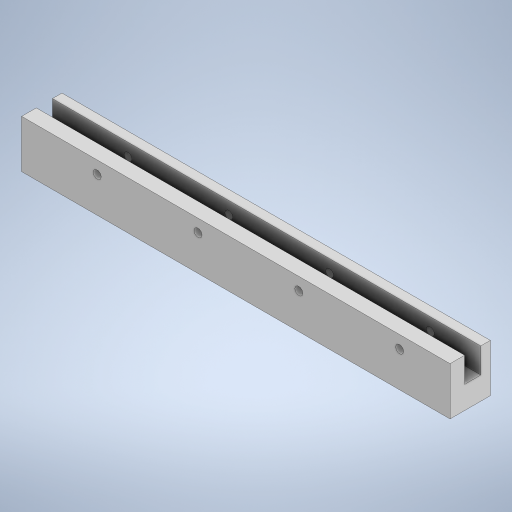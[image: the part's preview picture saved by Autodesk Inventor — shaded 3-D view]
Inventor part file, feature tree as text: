
AUTODESK INVENTOR PART (.ipt)
format: ipt  version: 2023 (Build 270158000, 158)  size: 327,680 bytes
history: native  units: mm
features: sketch x11, extrude x7, hole x4, other x1
ambient origin geometry x8: Origin, YZ Plane, XZ Plane, XY Plane, X Axis, Y Axis, Z Axis, Center Point
bodies: Body1 (feature_tree)
feature tree (23):
  other  "ソリッド1"
  extrude  "押し出し1"  Depth=180.0mm
  extrude  "押し出し2"  Depth=6.0mm
  extrude  "押し出し3"  Depth=17.0mm TaperAngle=0.0deg
  extrude  "押し出し4"  Depth=170.0mm
  extrude  "押し出し5"  Depth=6.0mm
  hole  "穴1"  [1 undecoded]
  hole  "穴2"  [1 undecoded]
  extrude  "押し出し6"  Depth=14.0mm TaperAngle=0.0deg
  hole  "穴3"  [1 undecoded]
  extrude  "押し出し7"  Depth=13.0mm TaperAngle=0.0deg
  hole  "穴4"  [1 undecoded]
  sketch  "スケッチ1"
  sketch  "スケッチ2"
  sketch  "スケッチ3"
  sketch  "スケッチ4"
  sketch  "スケッチ5"
  sketch  "スケッチ6"
  sketch  "スケッチ7"
  sketch  "スケッチ8"
  sketch  "スケッチ9"
  sketch  "スケッチ10"
  sketch  "スケッチ11"
note: 4 required parameter values undecoded (feature->parameter linkage not recoverable at this tier; creation-order binding heuristic only, values carry confidence <= 0.55)
